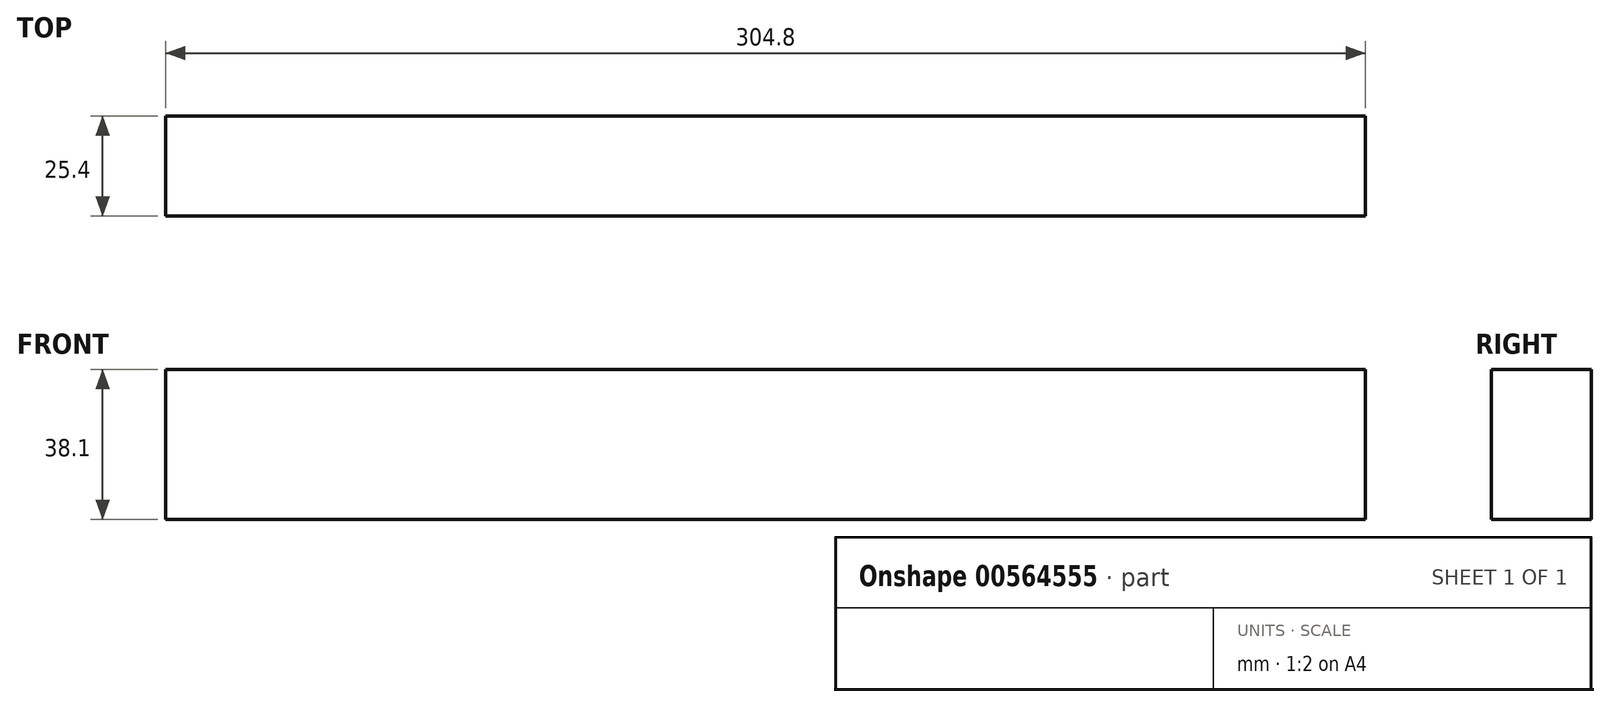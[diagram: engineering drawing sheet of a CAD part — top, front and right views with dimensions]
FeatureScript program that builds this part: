
annotation { "Feature Type Name" : "Feature", "Feature Type Description" : "" }
export const myFeature = defineFeature(function(context is Context, id is Id, definition is map)
    precondition{}
    {
        {
            var Q0;
            Q0=qCreatedBy(makeId("Front.planeOp"),FACE);
            var sketch = newSketch(context, id + "F0", { "sketchPlane" : qUnion([Q0])});
            skLineSegment(sketch, "E0.bottom", {"start": v(-248.7, 55.82) * mm, "end": v(56.1, 55.82) * mm});
            skLineSegment(sketch, "E0.top", {"start": v(-248.7, 17.72) * mm, "end": v(56.1, 17.72) * mm});
            skLineSegment(sketch, "E0.left", {"start": v(-248.7, 55.82) * mm, "end": v(-248.7, 17.72) * mm});
            skLineSegment(sketch, "E0.right", {"start": v(56.1, 55.82) * mm, "end": v(56.1, 17.72) * mm});
            skSolve(sketch);
        }
        {
            var Q0;
            Q0=makeQuery(id+"F0.imprint","IMPRINT",FACE,{"disambiguationData":[TD([[makeQuery(id+"F0.imprint","IMPRINT",EDGE,{"derivedFrom":sQuery(id+"F0.wireOp",EDGE,"E0.bottom")}),-1.0]])]});
            extrude(context, id + "F1", {"entities" : qUnion([Q0]), "depth" : 25.4 * mm, "offsetDistance" : 25.4 * mm});
        }
    });
